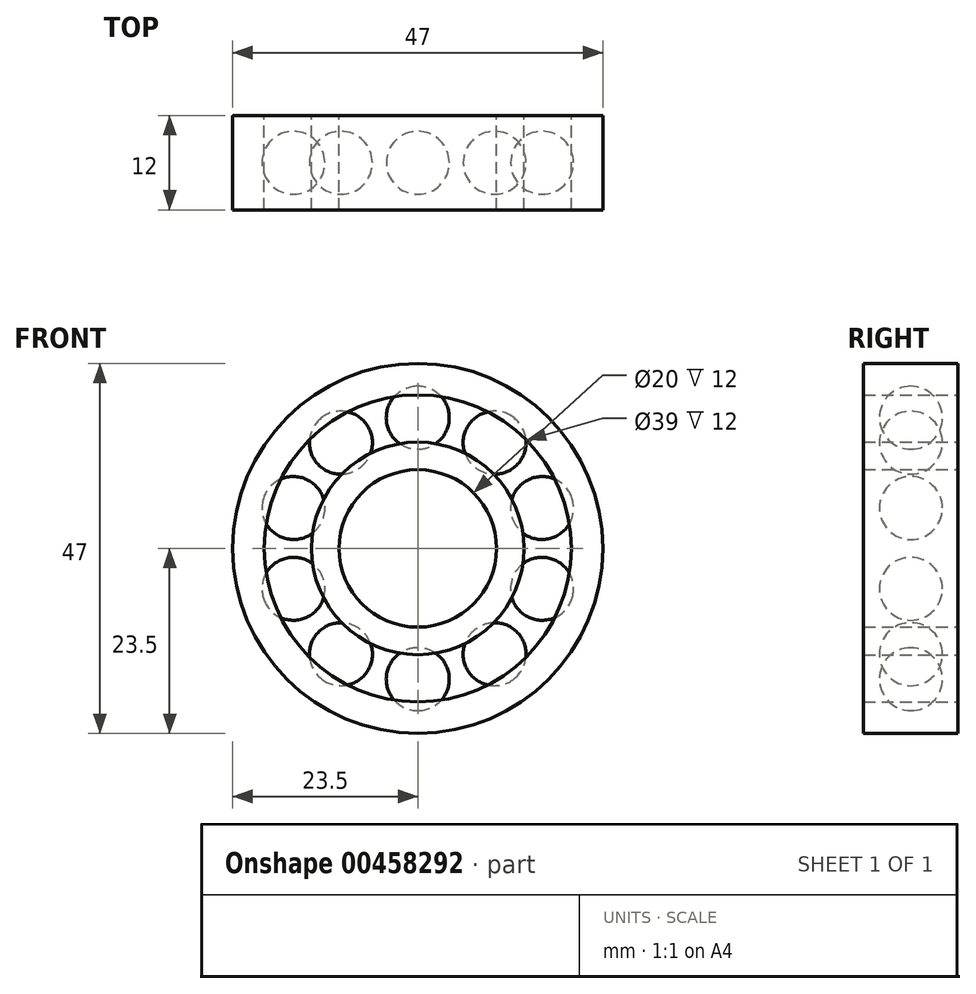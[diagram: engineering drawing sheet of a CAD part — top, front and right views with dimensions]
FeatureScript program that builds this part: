
annotation { "Feature Type Name" : "Feature", "Feature Type Description" : "" }
export const myFeature = defineFeature(function(context is Context, id is Id, definition is map)
    precondition{}
    {
        {
            var Q0;
            Q0=qCreatedBy(makeId("Front.planeOp"),FACE);
            var sketch = newSketch(context, id + "F0", { "sketchPlane" : qUnion([Q0])});
            skCircle(sketch, "E0", {"center": v(0, 0) * mm, "radius": 10 * mm});
            skCircle(sketch, "E1", {"center": v(0, 0) * mm, "radius": 13.5 * mm});
            skCircle(sketch, "E2", {"center": v(0, 0) * mm, "radius": 19.5 * mm});
            skCircle(sketch, "E3", {"center": v(0, 0) * mm, "radius": 23.5 * mm});
            skSolve(sketch);
        }
        {
            var Q0;
            Q0 = qSketchRegion(id + "F0", true);
            extrude(context, id + "F1", {"entities" : qUnion([Q0]), "depth" : 12 * mm});
        }
        {
            var Q0;
            Q0=makeQuery(id+"F0.imprint","IMPRINT",FACE,{"disambiguationData":[TD([[makeQuery(id+"F0.imprint","IMPRINT",EDGE,{"derivedFrom":sQuery(id+"F0.wireOp",EDGE,"E0")}),-1.0]])]});
            extrude(context, id + "F2", {"entities" : qUnion([Q0]), "depth" : 12 * mm});
        }
        {
            var Q0;
            Q0=qCreatedBy(makeId("Front.planeOp"),FACE);
            cPlane(context, id + "F3", {"entities" : qUnion([Q0]), "cplaneType" : CPlaneType.OFFSET, "offset" : 6 * mm, "width" : 150 * mm, "height" : 150 * mm});
        }
        {
            var Q0;
            Q0=qCreatedBy(id+"F3.planeOp",FACE);
            var sketch = newSketch(context, id + "F4", { "sketchPlane" : qUnion([Q0])});
            skArc(sketch, "E4", {"start": v(0, 12.6) * mm, "mid": v(4, 16.6) * mm, "end": v(0, 20.6) * mm});
            skLineSegment(sketch, "E5", {"start": v(0, 20.6) * mm, "end": v(0, 12.6) * mm});
            skPoint(sketch, "E6.orphan", {"position": v(0, 24.1) * mm});
            skSolve(sketch);
        }
        {
            var Q0;
            Q0=makeQuery(id+"F4.imprint","IMPRINT",FACE,{"disambiguationData":[TD([[makeQuery(id+"F4.imprint","IMPRINT",EDGE,{"derivedFrom":sQuery(id+"F4.wireOp",EDGE,"E4")}),1.0]])]});
            var Q1;
            Q1=sQuery(id+"F4.wireOp",EDGE,"E5");
            revolve(context, id + "F5", {"entities" : qUnion([Q0]), "axis" : qUnion([Q1]), "revolveType" : RevolveType.FULL});
        }
        {
            var Q0;
            Q0=qCreatedBy(makeId("Right.planeOp"),FACE);
            var sketch = newSketch(context, id + "F6", { "sketchPlane" : qUnion([Q0])});
            skLineSegment(sketch, "E7", {"start": v(-74.64, 0) * mm, "end": v(73.73, 0) * mm});
            skSolve(sketch);
        }
        {
            var Q0;
            Q0=makeQuery(id+"F5.opRevolve","SWEPT_BODY",BODY,{"disambiguationData":[OSD([sQuery(id+"F4.wireOp",EDGE,"E4"),sQuery(id+"F4.wireOp",EDGE,"E5")])]});
            var Q1;
            Q1=sQuery(id+"F6.wireOp",EDGE,"E7");
            circularPattern(context, id + "F7", {"entities" : qUnion([Q0]), "axis" : qUnion([Q1]), "angle" : 360 * degree, "instanceCount" : 10, "equalSpace" : true});
        }
    });
